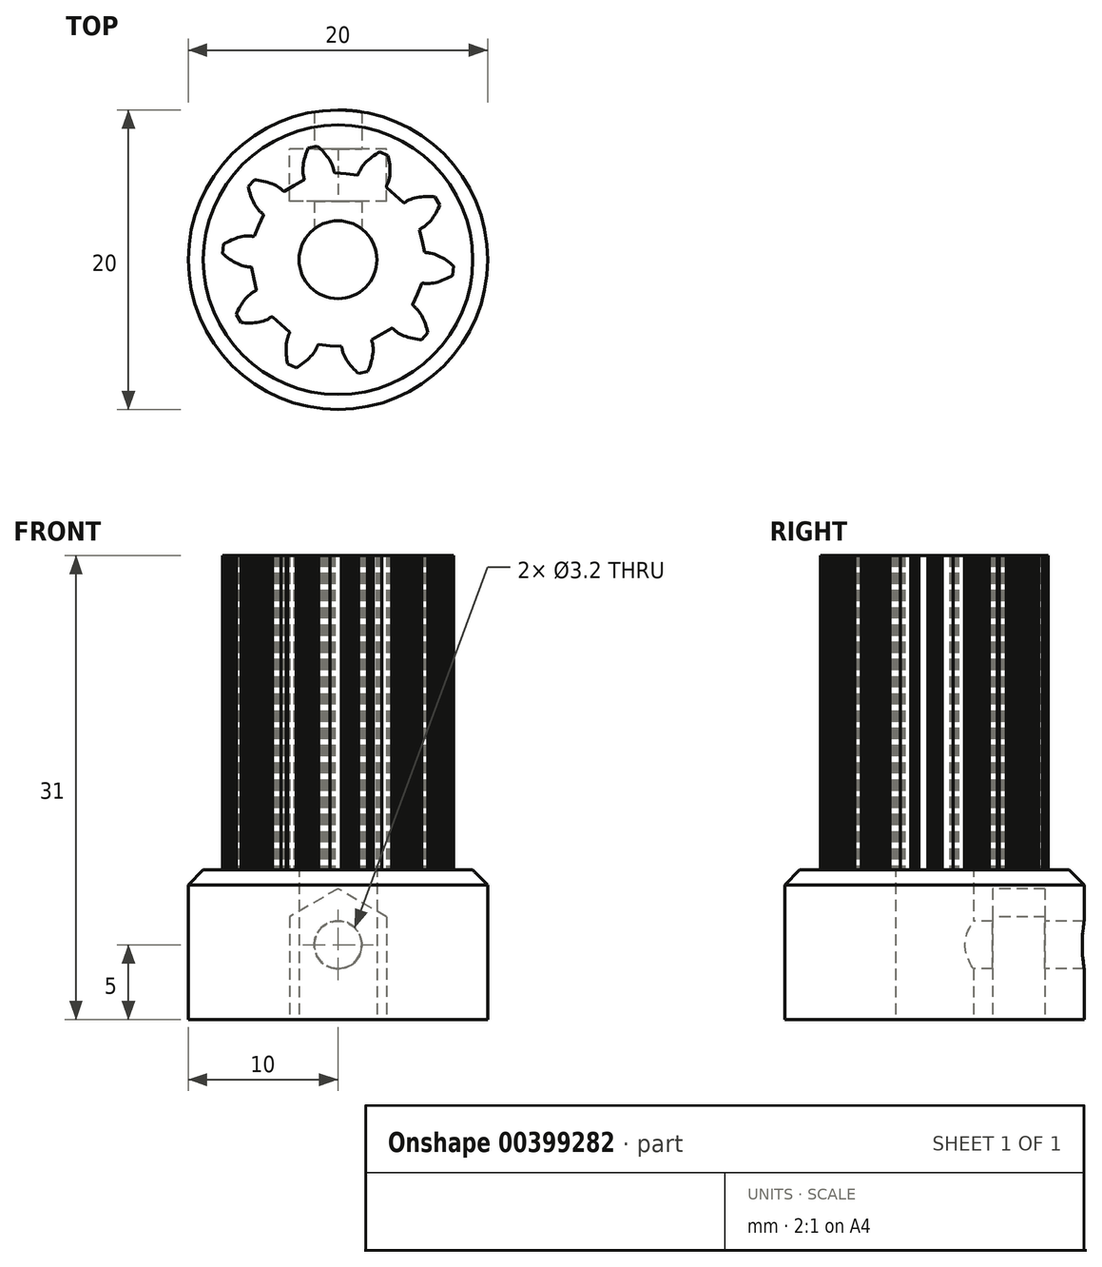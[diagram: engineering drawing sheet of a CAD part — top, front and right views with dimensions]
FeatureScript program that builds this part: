
annotation { "Feature Type Name" : "Feature", "Feature Type Description" : "" }
export const myFeature = defineFeature(function(context is Context, id is Id, definition is map)
    precondition{}
    {
        {
            var Q0;
            Q0=qCreatedBy(makeId("Top.planeOp"),FACE);
            var sketch = newSketch(context, id + "F0", { "sketchPlane" : qUnion([Q0])});
            skLineSegment(sketch, "E0", {"start": v(5.65, -3.86) * mm, "end": v(5.58, -3.73) * mm});
            skLineSegment(sketch, "E1", {"start": v(5.58, -3.73) * mm, "end": v(5.5, -3.6) * mm});
            skLineSegment(sketch, "E2", {"start": v(5.5, -3.6) * mm, "end": v(5.43, -3.49) * mm});
            skLineSegment(sketch, "E3", {"start": v(5.43, -3.49) * mm, "end": v(5.35, -3.37) * mm});
            skLineSegment(sketch, "E4", {"start": v(5.35, -3.37) * mm, "end": v(5.26, -3.27) * mm});
            skLineSegment(sketch, "E5", {"start": v(5.26, -3.27) * mm, "end": v(5.2, -3.22) * mm});
            skLineSegment(sketch, "E6", {"start": v(5.2, -3.22) * mm, "end": v(5.16, -3.18) * mm});
            skLineSegment(sketch, "E7", {"start": v(5.16, -3.18) * mm, "end": v(5.1, -3.14) * mm});
            skLineSegment(sketch, "E8", {"start": v(5.1, -3.14) * mm, "end": v(5.06, -3.1) * mm});
            skLineSegment(sketch, "E9", {"start": v(5.06, -3.1) * mm, "end": v(5.03, -3.07) * mm});
            skLineSegment(sketch, "E10", {"start": v(5.03, -3.07) * mm, "end": v(5.01, -3.05) * mm});
            skLineSegment(sketch, "E11", {"start": v(5.01, -3.05) * mm, "end": v(5, -3.02) * mm});
            skLineSegment(sketch, "E12", {"start": v(5, -3.02) * mm, "end": v(4.97, -2.98) * mm});
            skLineSegment(sketch, "E13", {"start": v(4.97, -2.98) * mm, "end": v(5.3, -2.3) * mm});
            skLineSegment(sketch, "E14", {"start": v(5.3, -2.3) * mm, "end": v(5.58, -1.58) * mm});
            skLineSegment(sketch, "E15", {"start": v(5.58, -1.58) * mm, "end": v(5.62, -1.57) * mm});
            skLineSegment(sketch, "E16", {"start": v(5.62, -1.57) * mm, "end": v(5.65, -1.57) * mm});
            skLineSegment(sketch, "E17", {"start": v(5.65, -1.57) * mm, "end": v(5.69, -1.57) * mm});
            skLineSegment(sketch, "E18", {"start": v(5.69, -1.57) * mm, "end": v(5.72, -1.57) * mm});
            skLineSegment(sketch, "E19", {"start": v(5.72, -1.57) * mm, "end": v(5.78, -1.58) * mm});
            skLineSegment(sketch, "E20", {"start": v(5.78, -1.58) * mm, "end": v(5.85, -1.59) * mm});
            skLineSegment(sketch, "E21", {"start": v(5.85, -1.59) * mm, "end": v(5.92, -1.6) * mm});
            skLineSegment(sketch, "E22", {"start": v(5.92, -1.6) * mm, "end": v(5.98, -1.6) * mm});
            skLineSegment(sketch, "E23", {"start": v(5.98, -1.6) * mm, "end": v(6.12, -1.59) * mm});
            skLineSegment(sketch, "E24", {"start": v(6.12, -1.59) * mm, "end": v(6.26, -1.57) * mm});
            skLineSegment(sketch, "E25", {"start": v(6.26, -1.57) * mm, "end": v(6.4, -1.55) * mm});
            skLineSegment(sketch, "E26", {"start": v(6.4, -1.55) * mm, "end": v(6.54, -1.52) * mm});
            skLineSegment(sketch, "E27", {"start": v(6.54, -1.52) * mm, "end": v(6.68, -1.48) * mm});
            skLineSegment(sketch, "E28", {"start": v(6.68, -1.48) * mm, "end": v(6.83, -1.43) * mm});
            skLineSegment(sketch, "E29", {"start": v(6.83, -1.43) * mm, "end": v(6.97, -1.38) * mm});
            skLineSegment(sketch, "E30", {"start": v(6.97, -1.38) * mm, "end": v(7.11, -1.32) * mm});
            skLineSegment(sketch, "E31", {"start": v(7.11, -1.32) * mm, "end": v(7.26, -1.25) * mm});
            skLineSegment(sketch, "E32", {"start": v(7.26, -1.25) * mm, "end": v(7.4, -1.18) * mm});
            skLineSegment(sketch, "E33", {"start": v(7.4, -1.18) * mm, "end": v(7.55, -1.1) * mm});
            skLineSegment(sketch, "E34", {"start": v(7.55, -1.1) * mm, "end": v(7.66, -1.03) * mm});
            skLineSegment(sketch, "E35", {"start": v(7.66, -1.03) * mm, "end": v(7.71, -0.42) * mm});
            skLineSegment(sketch, "E36", {"start": v(7.71, -0.42) * mm, "end": v(7.62, -0.34) * mm});
            skLineSegment(sketch, "E37", {"start": v(7.62, -0.34) * mm, "end": v(7.5, -0.23) * mm});
            skLineSegment(sketch, "E38", {"start": v(7.5, -0.23) * mm, "end": v(7.37, -0.13) * mm});
            skLineSegment(sketch, "E39", {"start": v(7.37, -0.13) * mm, "end": v(7.24, -0.04) * mm});
            skLineSegment(sketch, "E40", {"start": v(7.24, -0.04) * mm, "end": v(7.1, 0.05) * mm});
            skLineSegment(sketch, "E41", {"start": v(7.1, 0.05) * mm, "end": v(6.97, 0.13) * mm});
            skLineSegment(sketch, "E42", {"start": v(6.97, 0.13) * mm, "end": v(6.84, 0.2) * mm});
            skLineSegment(sketch, "E43", {"start": v(6.84, 0.2) * mm, "end": v(6.7, 0.27) * mm});
            skLineSegment(sketch, "E44", {"start": v(6.7, 0.27) * mm, "end": v(6.57, 0.32) * mm});
            skLineSegment(sketch, "E45", {"start": v(6.57, 0.32) * mm, "end": v(6.44, 0.37) * mm});
            skLineSegment(sketch, "E46", {"start": v(6.44, 0.37) * mm, "end": v(6.3, 0.41) * mm});
            skLineSegment(sketch, "E47", {"start": v(6.3, 0.41) * mm, "end": v(6.18, 0.44) * mm});
            skLineSegment(sketch, "E48", {"start": v(6.18, 0.44) * mm, "end": v(6.1, 0.45) * mm});
            skLineSegment(sketch, "E49", {"start": v(6.1, 0.45) * mm, "end": v(6.04, 0.46) * mm});
            skLineSegment(sketch, "E50", {"start": v(6.04, 0.46) * mm, "end": v(5.98, 0.47) * mm});
            skLineSegment(sketch, "E51", {"start": v(5.98, 0.47) * mm, "end": v(5.91, 0.47) * mm});
            skLineSegment(sketch, "E52", {"start": v(5.91, 0.47) * mm, "end": v(5.88, 0.47) * mm});
            skLineSegment(sketch, "E53", {"start": v(5.88, 0.47) * mm, "end": v(5.84, 0.48) * mm});
            skLineSegment(sketch, "E54", {"start": v(5.84, 0.48) * mm, "end": v(5.81, 0.5) * mm});
            skLineSegment(sketch, "E55", {"start": v(5.81, 0.5) * mm, "end": v(5.78, 0.51) * mm});
            skLineSegment(sketch, "E56", {"start": v(5.78, 0.51) * mm, "end": v(5.63, 1.26) * mm});
            skLineSegment(sketch, "E57", {"start": v(5.63, 1.26) * mm, "end": v(5.44, 2) * mm});
            skLineSegment(sketch, "E58", {"start": v(5.44, 2) * mm, "end": v(5.47, 2.03) * mm});
            skLineSegment(sketch, "E59", {"start": v(5.47, 2.03) * mm, "end": v(5.5, 2.05) * mm});
            skLineSegment(sketch, "E60", {"start": v(5.5, 2.05) * mm, "end": v(5.52, 2.07) * mm});
            skLineSegment(sketch, "E61", {"start": v(5.52, 2.07) * mm, "end": v(5.55, 2.1) * mm});
            skLineSegment(sketch, "E62", {"start": v(5.55, 2.1) * mm, "end": v(5.6, 2.12) * mm});
            skLineSegment(sketch, "E63", {"start": v(5.6, 2.12) * mm, "end": v(5.66, 2.15) * mm});
            skLineSegment(sketch, "E64", {"start": v(5.66, 2.15) * mm, "end": v(5.72, 2.19) * mm});
            skLineSegment(sketch, "E65", {"start": v(5.72, 2.19) * mm, "end": v(5.78, 2.23) * mm});
            skLineSegment(sketch, "E66", {"start": v(5.78, 2.23) * mm, "end": v(5.88, 2.31) * mm});
            skLineSegment(sketch, "E67", {"start": v(5.88, 2.31) * mm, "end": v(5.99, 2.4) * mm});
            skLineSegment(sketch, "E68", {"start": v(5.99, 2.4) * mm, "end": v(6.09, 2.5) * mm});
            skLineSegment(sketch, "E69", {"start": v(6.09, 2.5) * mm, "end": v(6.18, 2.62) * mm});
            skLineSegment(sketch, "E70", {"start": v(6.18, 2.62) * mm, "end": v(6.28, 2.73) * mm});
            skLineSegment(sketch, "E71", {"start": v(6.28, 2.73) * mm, "end": v(6.36, 2.85) * mm});
            skLineSegment(sketch, "E72", {"start": v(6.36, 2.85) * mm, "end": v(6.45, 2.98) * mm});
            skLineSegment(sketch, "E73", {"start": v(6.45, 2.98) * mm, "end": v(6.53, 3.12) * mm});
            skLineSegment(sketch, "E74", {"start": v(6.53, 3.12) * mm, "end": v(6.6, 3.25) * mm});
            skLineSegment(sketch, "E75", {"start": v(6.6, 3.25) * mm, "end": v(6.68, 3.4) * mm});
            skLineSegment(sketch, "E76", {"start": v(6.68, 3.4) * mm, "end": v(6.75, 3.55) * mm});
            skLineSegment(sketch, "E77", {"start": v(6.75, 3.55) * mm, "end": v(6.8, 3.66) * mm});
            skLineSegment(sketch, "E78", {"start": v(6.8, 3.66) * mm, "end": v(6.49, 4.2) * mm});
            skLineSegment(sketch, "E79", {"start": v(6.49, 4.2) * mm, "end": v(6.36, 4.2) * mm});
            skLineSegment(sketch, "E80", {"start": v(6.36, 4.2) * mm, "end": v(6.2, 4.22) * mm});
            skLineSegment(sketch, "E81", {"start": v(6.2, 4.22) * mm, "end": v(6.04, 4.22) * mm});
            skLineSegment(sketch, "E82", {"start": v(6.04, 4.22) * mm, "end": v(5.88, 4.22) * mm});
            skLineSegment(sketch, "E83", {"start": v(5.88, 4.22) * mm, "end": v(5.72, 4.22) * mm});
            skLineSegment(sketch, "E84", {"start": v(5.72, 4.22) * mm, "end": v(5.57, 4.2) * mm});
            skLineSegment(sketch, "E85", {"start": v(5.57, 4.2) * mm, "end": v(5.42, 4.18) * mm});
            skLineSegment(sketch, "E86", {"start": v(5.42, 4.18) * mm, "end": v(5.27, 4.16) * mm});
            skLineSegment(sketch, "E87", {"start": v(5.27, 4.16) * mm, "end": v(5.13, 4.13) * mm});
            skLineSegment(sketch, "E88", {"start": v(5.13, 4.13) * mm, "end": v(5, 4.09) * mm});
            skLineSegment(sketch, "E89", {"start": v(5, 4.09) * mm, "end": v(4.86, 4.04) * mm});
            skLineSegment(sketch, "E90", {"start": v(4.86, 4.04) * mm, "end": v(4.74, 3.99) * mm});
            skLineSegment(sketch, "E91", {"start": v(4.74, 3.99) * mm, "end": v(4.67, 3.96) * mm});
            skLineSegment(sketch, "E92", {"start": v(4.67, 3.96) * mm, "end": v(4.62, 3.93) * mm});
            skLineSegment(sketch, "E93", {"start": v(4.62, 3.93) * mm, "end": v(4.56, 3.89) * mm});
            skLineSegment(sketch, "E94", {"start": v(4.56, 3.89) * mm, "end": v(4.5, 3.85) * mm});
            skLineSegment(sketch, "E95", {"start": v(4.5, 3.85) * mm, "end": v(4.48, 3.84) * mm});
            skLineSegment(sketch, "E96", {"start": v(4.48, 3.84) * mm, "end": v(4.45, 3.82) * mm});
            skLineSegment(sketch, "E97", {"start": v(4.45, 3.82) * mm, "end": v(4.41, 3.81) * mm});
            skLineSegment(sketch, "E98", {"start": v(4.41, 3.81) * mm, "end": v(4.37, 3.8) * mm});
            skLineSegment(sketch, "E99", {"start": v(4.37, 3.8) * mm, "end": v(3.81, 4.33) * mm});
            skLineSegment(sketch, "E100", {"start": v(3.81, 4.33) * mm, "end": v(3.23, 4.82) * mm});
            skLineSegment(sketch, "E101", {"start": v(3.23, 4.82) * mm, "end": v(3.23, 4.86) * mm});
            skLineSegment(sketch, "E102", {"start": v(3.23, 4.86) * mm, "end": v(3.24, 4.9) * mm});
            skLineSegment(sketch, "E103", {"start": v(3.24, 4.9) * mm, "end": v(3.25, 4.92) * mm});
            skLineSegment(sketch, "E104", {"start": v(3.25, 4.92) * mm, "end": v(3.26, 4.95) * mm});
            skLineSegment(sketch, "E105", {"start": v(3.26, 4.95) * mm, "end": v(3.29, 5.01) * mm});
            skLineSegment(sketch, "E106", {"start": v(3.29, 5.01) * mm, "end": v(3.32, 5.07) * mm});
            skLineSegment(sketch, "E107", {"start": v(3.32, 5.07) * mm, "end": v(3.34, 5.13) * mm});
            skLineSegment(sketch, "E108", {"start": v(3.34, 5.13) * mm, "end": v(3.36, 5.2) * mm});
            skLineSegment(sketch, "E109", {"start": v(3.36, 5.2) * mm, "end": v(3.4, 5.33) * mm});
            skLineSegment(sketch, "E110", {"start": v(3.4, 5.33) * mm, "end": v(3.43, 5.47) * mm});
            skLineSegment(sketch, "E111", {"start": v(3.43, 5.47) * mm, "end": v(3.45, 5.6) * mm});
            skLineSegment(sketch, "E112", {"start": v(3.45, 5.6) * mm, "end": v(3.46, 5.75) * mm});
            skLineSegment(sketch, "E113", {"start": v(3.46, 5.75) * mm, "end": v(3.47, 5.9) * mm});
            skLineSegment(sketch, "E114", {"start": v(3.47, 5.9) * mm, "end": v(3.47, 6.05) * mm});
            skLineSegment(sketch, "E115", {"start": v(3.47, 6.05) * mm, "end": v(3.47, 6.2) * mm});
            skLineSegment(sketch, "E116", {"start": v(3.47, 6.2) * mm, "end": v(3.45, 6.36) * mm});
            skLineSegment(sketch, "E117", {"start": v(3.45, 6.36) * mm, "end": v(3.43, 6.52) * mm});
            skLineSegment(sketch, "E118", {"start": v(3.43, 6.52) * mm, "end": v(3.4, 6.68) * mm});
            skLineSegment(sketch, "E119", {"start": v(3.4, 6.68) * mm, "end": v(3.38, 6.84) * mm});
            skLineSegment(sketch, "E120", {"start": v(3.38, 6.84) * mm, "end": v(3.35, 6.96) * mm});
            skLineSegment(sketch, "E121", {"start": v(3.35, 6.96) * mm, "end": v(2.78, 7.2) * mm});
            skLineSegment(sketch, "E122", {"start": v(2.78, 7.2) * mm, "end": v(2.67, 7.14) * mm});
            skLineSegment(sketch, "E123", {"start": v(2.67, 7.14) * mm, "end": v(2.53, 7.06) * mm});
            skLineSegment(sketch, "E124", {"start": v(2.53, 7.06) * mm, "end": v(2.4, 6.96) * mm});
            skLineSegment(sketch, "E125", {"start": v(2.4, 6.96) * mm, "end": v(2.27, 6.87) * mm});
            skLineSegment(sketch, "E126", {"start": v(2.27, 6.87) * mm, "end": v(2.15, 6.77) * mm});
            skLineSegment(sketch, "E127", {"start": v(2.15, 6.77) * mm, "end": v(2.03, 6.67) * mm});
            skLineSegment(sketch, "E128", {"start": v(2.03, 6.67) * mm, "end": v(1.92, 6.57) * mm});
            skLineSegment(sketch, "E129", {"start": v(1.92, 6.57) * mm, "end": v(1.82, 6.46) * mm});
            skLineSegment(sketch, "E130", {"start": v(1.82, 6.46) * mm, "end": v(1.73, 6.35) * mm});
            skLineSegment(sketch, "E131", {"start": v(1.73, 6.35) * mm, "end": v(1.64, 6.24) * mm});
            skLineSegment(sketch, "E132", {"start": v(1.64, 6.24) * mm, "end": v(1.56, 6.13) * mm});
            skLineSegment(sketch, "E133", {"start": v(1.56, 6.13) * mm, "end": v(1.49, 6.01) * mm});
            skLineSegment(sketch, "E134", {"start": v(1.49, 6.01) * mm, "end": v(1.46, 5.95) * mm});
            skLineSegment(sketch, "E135", {"start": v(1.46, 5.95) * mm, "end": v(1.43, 5.89) * mm});
            skLineSegment(sketch, "E136", {"start": v(1.43, 5.89) * mm, "end": v(1.4, 5.83) * mm});
            skLineSegment(sketch, "E137", {"start": v(1.4, 5.83) * mm, "end": v(1.38, 5.77) * mm});
            skLineSegment(sketch, "E138", {"start": v(1.38, 5.77) * mm, "end": v(1.37, 5.74) * mm});
            skLineSegment(sketch, "E139", {"start": v(1.37, 5.74) * mm, "end": v(1.35, 5.7) * mm});
            skLineSegment(sketch, "E140", {"start": v(1.35, 5.7) * mm, "end": v(1.33, 5.68) * mm});
            skLineSegment(sketch, "E141", {"start": v(1.33, 5.68) * mm, "end": v(1.3, 5.65) * mm});
            skLineSegment(sketch, "E142", {"start": v(1.3, 5.65) * mm, "end": v(0.54, 5.74) * mm});
            skLineSegment(sketch, "E143", {"start": v(0.54, 5.74) * mm, "end": v(-0.22, 5.8) * mm});
            skLineSegment(sketch, "E144", {"start": v(-0.22, 5.8) * mm, "end": v(-0.24, 5.83) * mm});
            skLineSegment(sketch, "E145", {"start": v(-0.24, 5.83) * mm, "end": v(-0.26, 5.86) * mm});
            skLineSegment(sketch, "E146", {"start": v(-0.26, 5.86) * mm, "end": v(-0.27, 5.9) * mm});
            skLineSegment(sketch, "E147", {"start": v(-0.27, 5.9) * mm, "end": v(-0.28, 5.92) * mm});
            skLineSegment(sketch, "E148", {"start": v(-0.28, 5.92) * mm, "end": v(-0.29, 5.99) * mm});
            skLineSegment(sketch, "E149", {"start": v(-0.29, 5.99) * mm, "end": v(-0.3, 6.05) * mm});
            skLineSegment(sketch, "E150", {"start": v(-0.3, 6.05) * mm, "end": v(-0.31, 6.12) * mm});
            skLineSegment(sketch, "E151", {"start": v(-0.31, 6.12) * mm, "end": v(-0.33, 6.18) * mm});
            skLineSegment(sketch, "E152", {"start": v(-0.33, 6.18) * mm, "end": v(-0.38, 6.31) * mm});
            skLineSegment(sketch, "E153", {"start": v(-0.38, 6.31) * mm, "end": v(-0.44, 6.44) * mm});
            skLineSegment(sketch, "E154", {"start": v(-0.44, 6.44) * mm, "end": v(-0.5, 6.56) * mm});
            skLineSegment(sketch, "E155", {"start": v(-0.5, 6.56) * mm, "end": v(-0.58, 6.69) * mm});
            skLineSegment(sketch, "E156", {"start": v(-0.58, 6.69) * mm, "end": v(-0.66, 6.81) * mm});
            skLineSegment(sketch, "E157", {"start": v(-0.66, 6.81) * mm, "end": v(-0.75, 6.93) * mm});
            skLineSegment(sketch, "E158", {"start": v(-0.75, 6.93) * mm, "end": v(-0.84, 7.06) * mm});
            skLineSegment(sketch, "E159", {"start": v(-0.84, 7.06) * mm, "end": v(-0.94, 7.17) * mm});
            skLineSegment(sketch, "E160", {"start": v(-0.94, 7.17) * mm, "end": v(-1.05, 7.3) * mm});
            skLineSegment(sketch, "E161", {"start": v(-1.05, 7.3) * mm, "end": v(-1.17, 7.4) * mm});
            skLineSegment(sketch, "E162", {"start": v(-1.17, 7.4) * mm, "end": v(-1.29, 7.52) * mm});
            skLineSegment(sketch, "E163", {"start": v(-1.29, 7.52) * mm, "end": v(-1.38, 7.6) * mm});
            skLineSegment(sketch, "E164", {"start": v(-1.38, 7.6) * mm, "end": v(-1.98, 7.47) * mm});
            skLineSegment(sketch, "E165", {"start": v(-1.98, 7.47) * mm, "end": v(-2.04, 7.35) * mm});
            skLineSegment(sketch, "E166", {"start": v(-2.04, 7.35) * mm, "end": v(-2.1, 7.2) * mm});
            skLineSegment(sketch, "E167", {"start": v(-2.1, 7.2) * mm, "end": v(-2.15, 7.05) * mm});
            skLineSegment(sketch, "E168", {"start": v(-2.15, 7.05) * mm, "end": v(-2.2, 6.9) * mm});
            skLineSegment(sketch, "E169", {"start": v(-2.2, 6.9) * mm, "end": v(-2.24, 6.74) * mm});
            skLineSegment(sketch, "E170", {"start": v(-2.24, 6.74) * mm, "end": v(-2.28, 6.6) * mm});
            skLineSegment(sketch, "E171", {"start": v(-2.28, 6.6) * mm, "end": v(-2.3, 6.44) * mm});
            skLineSegment(sketch, "E172", {"start": v(-2.3, 6.44) * mm, "end": v(-2.33, 6.3) * mm});
            skLineSegment(sketch, "E173", {"start": v(-2.33, 6.3) * mm, "end": v(-2.34, 6.15) * mm});
            skLineSegment(sketch, "E174", {"start": v(-2.34, 6.15) * mm, "end": v(-2.34, 6.01) * mm});
            skLineSegment(sketch, "E175", {"start": v(-2.34, 6.01) * mm, "end": v(-2.34, 5.87) * mm});
            skLineSegment(sketch, "E176", {"start": v(-2.34, 5.87) * mm, "end": v(-2.33, 5.74) * mm});
            skLineSegment(sketch, "E177", {"start": v(-2.33, 5.74) * mm, "end": v(-2.32, 5.67) * mm});
            skLineSegment(sketch, "E178", {"start": v(-2.32, 5.67) * mm, "end": v(-2.3, 5.6) * mm});
            skLineSegment(sketch, "E179", {"start": v(-2.3, 5.6) * mm, "end": v(-2.29, 5.54) * mm});
            skLineSegment(sketch, "E180", {"start": v(-2.29, 5.54) * mm, "end": v(-2.27, 5.48) * mm});
            skLineSegment(sketch, "E181", {"start": v(-2.27, 5.48) * mm, "end": v(-2.27, 5.44) * mm});
            skLineSegment(sketch, "E182", {"start": v(-2.27, 5.44) * mm, "end": v(-2.26, 5.41) * mm});
            skLineSegment(sketch, "E183", {"start": v(-2.26, 5.41) * mm, "end": v(-2.26, 5.37) * mm});
            skLineSegment(sketch, "E184", {"start": v(-2.26, 5.37) * mm, "end": v(-2.27, 5.34) * mm});
            skLineSegment(sketch, "E185", {"start": v(-2.27, 5.34) * mm, "end": v(-2.94, 4.96) * mm});
            skLineSegment(sketch, "E186", {"start": v(-2.94, 4.96) * mm, "end": v(-3.58, 4.56) * mm});
            skLineSegment(sketch, "E187", {"start": v(-3.58, 4.56) * mm, "end": v(-3.62, 4.57) * mm});
            skLineSegment(sketch, "E188", {"start": v(-3.62, 4.57) * mm, "end": v(-3.65, 4.59) * mm});
            skLineSegment(sketch, "E189", {"start": v(-3.65, 4.59) * mm, "end": v(-3.68, 4.6) * mm});
            skLineSegment(sketch, "E190", {"start": v(-3.68, 4.6) * mm, "end": v(-3.7, 4.63) * mm});
            skLineSegment(sketch, "E191", {"start": v(-3.7, 4.63) * mm, "end": v(-3.75, 4.68) * mm});
            skLineSegment(sketch, "E192", {"start": v(-3.75, 4.68) * mm, "end": v(-3.8, 4.72) * mm});
            skLineSegment(sketch, "E193", {"start": v(-3.8, 4.72) * mm, "end": v(-3.85, 4.76) * mm});
            skLineSegment(sketch, "E194", {"start": v(-3.85, 4.76) * mm, "end": v(-3.9, 4.8) * mm});
            skLineSegment(sketch, "E195", {"start": v(-3.9, 4.8) * mm, "end": v(-4.02, 4.88) * mm});
            skLineSegment(sketch, "E196", {"start": v(-4.02, 4.88) * mm, "end": v(-4.14, 4.95) * mm});
            skLineSegment(sketch, "E197", {"start": v(-4.14, 4.95) * mm, "end": v(-4.27, 5.01) * mm});
            skLineSegment(sketch, "E198", {"start": v(-4.27, 5.01) * mm, "end": v(-4.4, 5.07) * mm});
            skLineSegment(sketch, "E199", {"start": v(-4.4, 5.07) * mm, "end": v(-4.54, 5.12) * mm});
            skLineSegment(sketch, "E200", {"start": v(-4.54, 5.12) * mm, "end": v(-4.68, 5.17) * mm});
            skLineSegment(sketch, "E201", {"start": v(-4.68, 5.17) * mm, "end": v(-4.83, 5.21) * mm});
            skLineSegment(sketch, "E202", {"start": v(-4.83, 5.21) * mm, "end": v(-4.98, 5.25) * mm});
            skLineSegment(sketch, "E203", {"start": v(-4.98, 5.25) * mm, "end": v(-5.14, 5.28) * mm});
            skLineSegment(sketch, "E204", {"start": v(-5.14, 5.28) * mm, "end": v(-5.3, 5.3) * mm});
            skLineSegment(sketch, "E205", {"start": v(-5.3, 5.3) * mm, "end": v(-5.46, 5.32) * mm});
            skLineSegment(sketch, "E206", {"start": v(-5.46, 5.32) * mm, "end": v(-5.59, 5.34) * mm});
            skLineSegment(sketch, "E207", {"start": v(-5.59, 5.34) * mm, "end": v(-6, 4.87) * mm});
            skLineSegment(sketch, "E208", {"start": v(-6, 4.87) * mm, "end": v(-5.97, 4.75) * mm});
            skLineSegment(sketch, "E209", {"start": v(-5.97, 4.75) * mm, "end": v(-5.93, 4.6) * mm});
            skLineSegment(sketch, "E210", {"start": v(-5.93, 4.6) * mm, "end": v(-5.88, 4.44) * mm});
            skLineSegment(sketch, "E211", {"start": v(-5.88, 4.44) * mm, "end": v(-5.83, 4.28) * mm});
            skLineSegment(sketch, "E212", {"start": v(-5.83, 4.28) * mm, "end": v(-5.78, 4.14) * mm});
            skLineSegment(sketch, "E213", {"start": v(-5.78, 4.14) * mm, "end": v(-5.72, 4) * mm});
            skLineSegment(sketch, "E214", {"start": v(-5.72, 4) * mm, "end": v(-5.65, 3.86) * mm});
            skLineSegment(sketch, "E215", {"start": v(-5.65, 3.86) * mm, "end": v(-5.58, 3.73) * mm});
            skLineSegment(sketch, "E216", {"start": v(-5.58, 3.73) * mm, "end": v(-5.5, 3.6) * mm});
            skLineSegment(sketch, "E217", {"start": v(-5.5, 3.6) * mm, "end": v(-5.43, 3.49) * mm});
            skLineSegment(sketch, "E218", {"start": v(-5.43, 3.49) * mm, "end": v(-5.35, 3.37) * mm});
            skLineSegment(sketch, "E219", {"start": v(-5.35, 3.37) * mm, "end": v(-5.26, 3.27) * mm});
            skLineSegment(sketch, "E220", {"start": v(-5.26, 3.27) * mm, "end": v(-5.2, 3.22) * mm});
            skLineSegment(sketch, "E221", {"start": v(-5.2, 3.22) * mm, "end": v(-5.16, 3.18) * mm});
            skLineSegment(sketch, "E222", {"start": v(-5.16, 3.18) * mm, "end": v(-5.1, 3.14) * mm});
            skLineSegment(sketch, "E223", {"start": v(-5.1, 3.14) * mm, "end": v(-5.06, 3.1) * mm});
            skLineSegment(sketch, "E224", {"start": v(-5.06, 3.1) * mm, "end": v(-5.03, 3.07) * mm});
            skLineSegment(sketch, "E225", {"start": v(-5.03, 3.07) * mm, "end": v(-5.01, 3.05) * mm});
            skLineSegment(sketch, "E226", {"start": v(-5.01, 3.05) * mm, "end": v(-5, 3.02) * mm});
            skLineSegment(sketch, "E227", {"start": v(-5, 3.02) * mm, "end": v(-4.97, 2.98) * mm});
            skLineSegment(sketch, "E228", {"start": v(-4.97, 2.98) * mm, "end": v(-5.3, 2.3) * mm});
            skLineSegment(sketch, "E229", {"start": v(-5.3, 2.3) * mm, "end": v(-5.58, 1.58) * mm});
            skLineSegment(sketch, "E230", {"start": v(-5.58, 1.58) * mm, "end": v(-5.62, 1.57) * mm});
            skLineSegment(sketch, "E231", {"start": v(-5.62, 1.57) * mm, "end": v(-5.65, 1.57) * mm});
            skLineSegment(sketch, "E232", {"start": v(-5.65, 1.57) * mm, "end": v(-5.69, 1.57) * mm});
            skLineSegment(sketch, "E233", {"start": v(-5.69, 1.57) * mm, "end": v(-5.72, 1.57) * mm});
            skLineSegment(sketch, "E234", {"start": v(-5.72, 1.57) * mm, "end": v(-5.78, 1.58) * mm});
            skLineSegment(sketch, "E235", {"start": v(-5.78, 1.58) * mm, "end": v(-5.85, 1.59) * mm});
            skLineSegment(sketch, "E236", {"start": v(-5.85, 1.59) * mm, "end": v(-5.92, 1.6) * mm});
            skLineSegment(sketch, "E237", {"start": v(-5.92, 1.6) * mm, "end": v(-5.98, 1.6) * mm});
            skLineSegment(sketch, "E238", {"start": v(-5.98, 1.6) * mm, "end": v(-6.12, 1.59) * mm});
            skLineSegment(sketch, "E239", {"start": v(-6.12, 1.59) * mm, "end": v(-6.26, 1.57) * mm});
            skLineSegment(sketch, "E240", {"start": v(-6.26, 1.57) * mm, "end": v(-6.4, 1.55) * mm});
            skLineSegment(sketch, "E241", {"start": v(-6.4, 1.55) * mm, "end": v(-6.54, 1.52) * mm});
            skLineSegment(sketch, "E242", {"start": v(-6.54, 1.52) * mm, "end": v(-6.68, 1.48) * mm});
            skLineSegment(sketch, "E243", {"start": v(-6.68, 1.48) * mm, "end": v(-6.83, 1.43) * mm});
            skLineSegment(sketch, "E244", {"start": v(-6.83, 1.43) * mm, "end": v(-6.97, 1.38) * mm});
            skLineSegment(sketch, "E245", {"start": v(-6.97, 1.38) * mm, "end": v(-7.11, 1.32) * mm});
            skLineSegment(sketch, "E246", {"start": v(-7.11, 1.32) * mm, "end": v(-7.26, 1.25) * mm});
            skLineSegment(sketch, "E247", {"start": v(-7.26, 1.25) * mm, "end": v(-7.4, 1.18) * mm});
            skLineSegment(sketch, "E248", {"start": v(-7.4, 1.18) * mm, "end": v(-7.55, 1.1) * mm});
            skLineSegment(sketch, "E249", {"start": v(-7.55, 1.1) * mm, "end": v(-7.66, 1.03) * mm});
            skLineSegment(sketch, "E250", {"start": v(-7.66, 1.03) * mm, "end": v(-7.71, 0.42) * mm});
            skLineSegment(sketch, "E251", {"start": v(-7.71, 0.42) * mm, "end": v(-7.62, 0.34) * mm});
            skLineSegment(sketch, "E252", {"start": v(-7.62, 0.34) * mm, "end": v(-7.5, 0.23) * mm});
            skLineSegment(sketch, "E253", {"start": v(-7.5, 0.23) * mm, "end": v(-7.37, 0.13) * mm});
            skLineSegment(sketch, "E254", {"start": v(-7.37, 0.13) * mm, "end": v(-7.24, 0.04) * mm});
            skLineSegment(sketch, "E255", {"start": v(-7.24, 0.04) * mm, "end": v(-7.1, -0.05) * mm});
            skLineSegment(sketch, "E256", {"start": v(-7.1, -0.05) * mm, "end": v(-6.97, -0.13) * mm});
            skLineSegment(sketch, "E257", {"start": v(-6.97, -0.13) * mm, "end": v(-6.84, -0.2) * mm});
            skLineSegment(sketch, "E258", {"start": v(-6.84, -0.2) * mm, "end": v(-6.7, -0.27) * mm});
            skLineSegment(sketch, "E259", {"start": v(-6.7, -0.27) * mm, "end": v(-6.58, -0.32) * mm});
            skLineSegment(sketch, "E260", {"start": v(-6.58, -0.32) * mm, "end": v(-6.44, -0.37) * mm});
            skLineSegment(sketch, "E261", {"start": v(-6.44, -0.37) * mm, "end": v(-6.3, -0.41) * mm});
            skLineSegment(sketch, "E262", {"start": v(-6.3, -0.41) * mm, "end": v(-6.18, -0.44) * mm});
            skLineSegment(sketch, "E263", {"start": v(-6.18, -0.44) * mm, "end": v(-6.1, -0.45) * mm});
            skLineSegment(sketch, "E264", {"start": v(-6.1, -0.45) * mm, "end": v(-6.04, -0.46) * mm});
            skLineSegment(sketch, "E265", {"start": v(-6.04, -0.46) * mm, "end": v(-5.98, -0.46) * mm});
            skLineSegment(sketch, "E266", {"start": v(-5.98, -0.46) * mm, "end": v(-5.91, -0.47) * mm});
            skLineSegment(sketch, "E267", {"start": v(-5.91, -0.47) * mm, "end": v(-5.88, -0.47) * mm});
            skLineSegment(sketch, "E268", {"start": v(-5.88, -0.47) * mm, "end": v(-5.84, -0.48) * mm});
            skLineSegment(sketch, "E269", {"start": v(-5.84, -0.48) * mm, "end": v(-5.81, -0.5) * mm});
            skLineSegment(sketch, "E270", {"start": v(-5.81, -0.5) * mm, "end": v(-5.78, -0.51) * mm});
            skLineSegment(sketch, "E271", {"start": v(-5.78, -0.51) * mm, "end": v(-5.63, -1.26) * mm});
            skLineSegment(sketch, "E272", {"start": v(-5.63, -1.26) * mm, "end": v(-5.44, -2) * mm});
            skLineSegment(sketch, "E273", {"start": v(-5.44, -2) * mm, "end": v(-5.47, -2.03) * mm});
            skLineSegment(sketch, "E274", {"start": v(-5.47, -2.03) * mm, "end": v(-5.5, -2.05) * mm});
            skLineSegment(sketch, "E275", {"start": v(-5.5, -2.05) * mm, "end": v(-5.52, -2.07) * mm});
            skLineSegment(sketch, "E276", {"start": v(-5.52, -2.07) * mm, "end": v(-5.55, -2.1) * mm});
            skLineSegment(sketch, "E277", {"start": v(-5.55, -2.1) * mm, "end": v(-5.6, -2.12) * mm});
            skLineSegment(sketch, "E278", {"start": v(-5.6, -2.12) * mm, "end": v(-5.66, -2.15) * mm});
            skLineSegment(sketch, "E279", {"start": v(-5.66, -2.15) * mm, "end": v(-5.72, -2.19) * mm});
            skLineSegment(sketch, "E280", {"start": v(-5.72, -2.19) * mm, "end": v(-5.78, -2.23) * mm});
            skLineSegment(sketch, "E281", {"start": v(-5.78, -2.23) * mm, "end": v(-5.88, -2.31) * mm});
            skLineSegment(sketch, "E282", {"start": v(-5.88, -2.31) * mm, "end": v(-5.99, -2.4) * mm});
            skLineSegment(sketch, "E283", {"start": v(-5.99, -2.4) * mm, "end": v(-6.09, -2.5) * mm});
            skLineSegment(sketch, "E284", {"start": v(-6.09, -2.5) * mm, "end": v(-6.18, -2.62) * mm});
            skLineSegment(sketch, "E285", {"start": v(-6.18, -2.62) * mm, "end": v(-6.28, -2.73) * mm});
            skLineSegment(sketch, "E286", {"start": v(-6.28, -2.73) * mm, "end": v(-6.36, -2.85) * mm});
            skLineSegment(sketch, "E287", {"start": v(-6.36, -2.85) * mm, "end": v(-6.45, -2.98) * mm});
            skLineSegment(sketch, "E288", {"start": v(-6.45, -2.98) * mm, "end": v(-6.53, -3.12) * mm});
            skLineSegment(sketch, "E289", {"start": v(-6.53, -3.12) * mm, "end": v(-6.6, -3.25) * mm});
            skLineSegment(sketch, "E290", {"start": v(-6.6, -3.25) * mm, "end": v(-6.68, -3.4) * mm});
            skLineSegment(sketch, "E291", {"start": v(-6.68, -3.4) * mm, "end": v(-6.75, -3.55) * mm});
            skLineSegment(sketch, "E292", {"start": v(-6.75, -3.55) * mm, "end": v(-6.8, -3.66) * mm});
            skLineSegment(sketch, "E293", {"start": v(-6.8, -3.66) * mm, "end": v(-6.49, -4.2) * mm});
            skLineSegment(sketch, "E294", {"start": v(-6.49, -4.2) * mm, "end": v(-6.36, -4.2) * mm});
            skLineSegment(sketch, "E295", {"start": v(-6.36, -4.2) * mm, "end": v(-6.2, -4.22) * mm});
            skLineSegment(sketch, "E296", {"start": v(-6.2, -4.22) * mm, "end": v(-6.04, -4.22) * mm});
            skLineSegment(sketch, "E297", {"start": v(-6.04, -4.22) * mm, "end": v(-5.88, -4.22) * mm});
            skLineSegment(sketch, "E298", {"start": v(-5.88, -4.22) * mm, "end": v(-5.72, -4.22) * mm});
            skLineSegment(sketch, "E299", {"start": v(-5.72, -4.22) * mm, "end": v(-5.57, -4.2) * mm});
            skLineSegment(sketch, "E300", {"start": v(-5.57, -4.2) * mm, "end": v(-5.42, -4.18) * mm});
            skLineSegment(sketch, "E301", {"start": v(-5.42, -4.18) * mm, "end": v(-5.27, -4.16) * mm});
            skLineSegment(sketch, "E302", {"start": v(-5.27, -4.16) * mm, "end": v(-5.13, -4.13) * mm});
            skLineSegment(sketch, "E303", {"start": v(-5.13, -4.13) * mm, "end": v(-5, -4.09) * mm});
            skLineSegment(sketch, "E304", {"start": v(-5, -4.09) * mm, "end": v(-4.86, -4.04) * mm});
            skLineSegment(sketch, "E305", {"start": v(-4.86, -4.04) * mm, "end": v(-4.74, -3.99) * mm});
            skLineSegment(sketch, "E306", {"start": v(-4.74, -3.99) * mm, "end": v(-4.68, -3.96) * mm});
            skLineSegment(sketch, "E307", {"start": v(-4.68, -3.96) * mm, "end": v(-4.62, -3.93) * mm});
            skLineSegment(sketch, "E308", {"start": v(-4.62, -3.93) * mm, "end": v(-4.56, -3.89) * mm});
            skLineSegment(sketch, "E309", {"start": v(-4.56, -3.89) * mm, "end": v(-4.5, -3.85) * mm});
            skLineSegment(sketch, "E310", {"start": v(-4.5, -3.85) * mm, "end": v(-4.48, -3.84) * mm});
            skLineSegment(sketch, "E311", {"start": v(-4.48, -3.84) * mm, "end": v(-4.45, -3.82) * mm});
            skLineSegment(sketch, "E312", {"start": v(-4.45, -3.82) * mm, "end": v(-4.41, -3.81) * mm});
            skLineSegment(sketch, "E313", {"start": v(-4.41, -3.81) * mm, "end": v(-4.37, -3.8) * mm});
            skLineSegment(sketch, "E314", {"start": v(-4.37, -3.8) * mm, "end": v(-3.81, -4.33) * mm});
            skLineSegment(sketch, "E315", {"start": v(-3.81, -4.33) * mm, "end": v(-3.23, -4.82) * mm});
            skLineSegment(sketch, "E316", {"start": v(-3.23, -4.82) * mm, "end": v(-3.23, -4.86) * mm});
            skLineSegment(sketch, "E317", {"start": v(-3.23, -4.86) * mm, "end": v(-3.24, -4.9) * mm});
            skLineSegment(sketch, "E318", {"start": v(-3.24, -4.9) * mm, "end": v(-3.25, -4.92) * mm});
            skLineSegment(sketch, "E319", {"start": v(-3.25, -4.92) * mm, "end": v(-3.26, -4.95) * mm});
            skLineSegment(sketch, "E320", {"start": v(-3.26, -4.95) * mm, "end": v(-3.29, -5.01) * mm});
            skLineSegment(sketch, "E321", {"start": v(-3.29, -5.01) * mm, "end": v(-3.32, -5.07) * mm});
            skLineSegment(sketch, "E322", {"start": v(-3.32, -5.07) * mm, "end": v(-3.34, -5.13) * mm});
            skLineSegment(sketch, "E323", {"start": v(-3.34, -5.13) * mm, "end": v(-3.36, -5.2) * mm});
            skLineSegment(sketch, "E324", {"start": v(-3.36, -5.2) * mm, "end": v(-3.4, -5.33) * mm});
            skLineSegment(sketch, "E325", {"start": v(-3.4, -5.33) * mm, "end": v(-3.43, -5.47) * mm});
            skLineSegment(sketch, "E326", {"start": v(-3.43, -5.47) * mm, "end": v(-3.45, -5.6) * mm});
            skLineSegment(sketch, "E327", {"start": v(-3.45, -5.6) * mm, "end": v(-3.46, -5.75) * mm});
            skLineSegment(sketch, "E328", {"start": v(-3.46, -5.75) * mm, "end": v(-3.47, -5.9) * mm});
            skLineSegment(sketch, "E329", {"start": v(-3.47, -5.9) * mm, "end": v(-3.47, -6.05) * mm});
            skLineSegment(sketch, "E330", {"start": v(-3.47, -6.05) * mm, "end": v(-3.47, -6.2) * mm});
            skLineSegment(sketch, "E331", {"start": v(-3.47, -6.2) * mm, "end": v(-3.45, -6.36) * mm});
            skLineSegment(sketch, "E332", {"start": v(-3.45, -6.36) * mm, "end": v(-3.43, -6.52) * mm});
            skLineSegment(sketch, "E333", {"start": v(-3.43, -6.52) * mm, "end": v(-3.4, -6.68) * mm});
            skLineSegment(sketch, "E334", {"start": v(-3.4, -6.68) * mm, "end": v(-3.38, -6.84) * mm});
            skLineSegment(sketch, "E335", {"start": v(-3.38, -6.84) * mm, "end": v(-3.35, -6.96) * mm});
            skLineSegment(sketch, "E336", {"start": v(-3.35, -6.96) * mm, "end": v(-2.78, -7.2) * mm});
            skLineSegment(sketch, "E337", {"start": v(-2.78, -7.2) * mm, "end": v(-2.67, -7.14) * mm});
            skLineSegment(sketch, "E338", {"start": v(-2.67, -7.14) * mm, "end": v(-2.53, -7.06) * mm});
            skLineSegment(sketch, "E339", {"start": v(-2.53, -7.06) * mm, "end": v(-2.4, -6.96) * mm});
            skLineSegment(sketch, "E340", {"start": v(-2.4, -6.96) * mm, "end": v(-2.27, -6.87) * mm});
            skLineSegment(sketch, "E341", {"start": v(-2.27, -6.87) * mm, "end": v(-2.15, -6.77) * mm});
            skLineSegment(sketch, "E342", {"start": v(-2.15, -6.77) * mm, "end": v(-2.03, -6.67) * mm});
            skLineSegment(sketch, "E343", {"start": v(-2.03, -6.67) * mm, "end": v(-1.92, -6.57) * mm});
            skLineSegment(sketch, "E344", {"start": v(-1.92, -6.57) * mm, "end": v(-1.82, -6.46) * mm});
            skLineSegment(sketch, "E345", {"start": v(-1.82, -6.46) * mm, "end": v(-1.73, -6.35) * mm});
            skLineSegment(sketch, "E346", {"start": v(-1.73, -6.35) * mm, "end": v(-1.64, -6.24) * mm});
            skLineSegment(sketch, "E347", {"start": v(-1.64, -6.24) * mm, "end": v(-1.56, -6.13) * mm});
            skLineSegment(sketch, "E348", {"start": v(-1.56, -6.13) * mm, "end": v(-1.49, -6) * mm});
            skLineSegment(sketch, "E349", {"start": v(-1.49, -6) * mm, "end": v(-1.46, -5.95) * mm});
            skLineSegment(sketch, "E350", {"start": v(-1.46, -5.95) * mm, "end": v(-1.43, -5.89) * mm});
            skLineSegment(sketch, "E351", {"start": v(-1.43, -5.89) * mm, "end": v(-1.4, -5.83) * mm});
            skLineSegment(sketch, "E352", {"start": v(-1.4, -5.83) * mm, "end": v(-1.38, -5.77) * mm});
            skLineSegment(sketch, "E353", {"start": v(-1.38, -5.77) * mm, "end": v(-1.37, -5.74) * mm});
            skLineSegment(sketch, "E354", {"start": v(-1.37, -5.74) * mm, "end": v(-1.35, -5.7) * mm});
            skLineSegment(sketch, "E355", {"start": v(-1.35, -5.7) * mm, "end": v(-1.33, -5.68) * mm});
            skLineSegment(sketch, "E356", {"start": v(-1.33, -5.68) * mm, "end": v(-1.3, -5.65) * mm});
            skLineSegment(sketch, "E357", {"start": v(-1.3, -5.65) * mm, "end": v(-0.54, -5.74) * mm});
            skLineSegment(sketch, "E358", {"start": v(-0.54, -5.74) * mm, "end": v(0.22, -5.8) * mm});
            skLineSegment(sketch, "E359", {"start": v(0.22, -5.8) * mm, "end": v(0.24, -5.83) * mm});
            skLineSegment(sketch, "E360", {"start": v(0.24, -5.83) * mm, "end": v(0.26, -5.86) * mm});
            skLineSegment(sketch, "E361", {"start": v(0.26, -5.86) * mm, "end": v(0.27, -5.9) * mm});
            skLineSegment(sketch, "E362", {"start": v(0.27, -5.9) * mm, "end": v(0.28, -5.92) * mm});
            skLineSegment(sketch, "E363", {"start": v(0.28, -5.92) * mm, "end": v(0.29, -5.99) * mm});
            skLineSegment(sketch, "E364", {"start": v(0.29, -5.99) * mm, "end": v(0.3, -6.05) * mm});
            skLineSegment(sketch, "E365", {"start": v(0.3, -6.05) * mm, "end": v(0.31, -6.12) * mm});
            skLineSegment(sketch, "E366", {"start": v(0.31, -6.12) * mm, "end": v(0.33, -6.18) * mm});
            skLineSegment(sketch, "E367", {"start": v(0.33, -6.18) * mm, "end": v(0.38, -6.31) * mm});
            skLineSegment(sketch, "E368", {"start": v(0.38, -6.31) * mm, "end": v(0.44, -6.44) * mm});
            skLineSegment(sketch, "E369", {"start": v(0.44, -6.44) * mm, "end": v(0.5, -6.56) * mm});
            skLineSegment(sketch, "E370", {"start": v(0.5, -6.56) * mm, "end": v(0.58, -6.69) * mm});
            skLineSegment(sketch, "E371", {"start": v(0.58, -6.69) * mm, "end": v(0.66, -6.81) * mm});
            skLineSegment(sketch, "E372", {"start": v(0.66, -6.81) * mm, "end": v(0.75, -6.93) * mm});
            skLineSegment(sketch, "E373", {"start": v(0.75, -6.93) * mm, "end": v(0.84, -7.06) * mm});
            skLineSegment(sketch, "E374", {"start": v(0.84, -7.06) * mm, "end": v(0.94, -7.17) * mm});
            skLineSegment(sketch, "E375", {"start": v(0.94, -7.17) * mm, "end": v(1.05, -7.3) * mm});
            skLineSegment(sketch, "E376", {"start": v(1.05, -7.3) * mm, "end": v(1.17, -7.4) * mm});
            skLineSegment(sketch, "E377", {"start": v(1.17, -7.4) * mm, "end": v(1.29, -7.52) * mm});
            skLineSegment(sketch, "E378", {"start": v(1.29, -7.52) * mm, "end": v(1.38, -7.6) * mm});
            skLineSegment(sketch, "E379", {"start": v(1.38, -7.6) * mm, "end": v(1.98, -7.47) * mm});
            skLineSegment(sketch, "E380", {"start": v(1.98, -7.47) * mm, "end": v(2.04, -7.35) * mm});
            skLineSegment(sketch, "E381", {"start": v(2.04, -7.35) * mm, "end": v(2.1, -7.2) * mm});
            skLineSegment(sketch, "E382", {"start": v(2.1, -7.2) * mm, "end": v(2.15, -7.05) * mm});
            skLineSegment(sketch, "E383", {"start": v(2.15, -7.05) * mm, "end": v(2.2, -6.9) * mm});
            skLineSegment(sketch, "E384", {"start": v(2.2, -6.9) * mm, "end": v(2.24, -6.74) * mm});
            skLineSegment(sketch, "E385", {"start": v(2.24, -6.74) * mm, "end": v(2.28, -6.6) * mm});
            skLineSegment(sketch, "E386", {"start": v(2.28, -6.6) * mm, "end": v(2.3, -6.44) * mm});
            skLineSegment(sketch, "E387", {"start": v(2.3, -6.44) * mm, "end": v(2.33, -6.3) * mm});
            skLineSegment(sketch, "E388", {"start": v(2.33, -6.3) * mm, "end": v(2.34, -6.15) * mm});
            skLineSegment(sketch, "E389", {"start": v(2.34, -6.15) * mm, "end": v(2.34, -6.01) * mm});
            skLineSegment(sketch, "E390", {"start": v(2.34, -6.01) * mm, "end": v(2.34, -5.87) * mm});
            skLineSegment(sketch, "E391", {"start": v(2.34, -5.87) * mm, "end": v(2.33, -5.74) * mm});
            skLineSegment(sketch, "E392", {"start": v(2.33, -5.74) * mm, "end": v(2.32, -5.67) * mm});
            skLineSegment(sketch, "E393", {"start": v(2.32, -5.67) * mm, "end": v(2.3, -5.6) * mm});
            skLineSegment(sketch, "E394", {"start": v(2.3, -5.6) * mm, "end": v(2.29, -5.54) * mm});
            skLineSegment(sketch, "E395", {"start": v(2.29, -5.54) * mm, "end": v(2.27, -5.48) * mm});
            skLineSegment(sketch, "E396", {"start": v(2.27, -5.48) * mm, "end": v(2.27, -5.44) * mm});
            skLineSegment(sketch, "E397", {"start": v(2.27, -5.44) * mm, "end": v(2.26, -5.41) * mm});
            skLineSegment(sketch, "E398", {"start": v(2.26, -5.41) * mm, "end": v(2.26, -5.37) * mm});
            skLineSegment(sketch, "E399", {"start": v(2.26, -5.37) * mm, "end": v(2.27, -5.34) * mm});
            skLineSegment(sketch, "E400", {"start": v(2.27, -5.34) * mm, "end": v(2.94, -4.96) * mm});
            skLineSegment(sketch, "E401", {"start": v(2.94, -4.96) * mm, "end": v(3.58, -4.56) * mm});
            skLineSegment(sketch, "E402", {"start": v(3.58, -4.56) * mm, "end": v(3.62, -4.57) * mm});
            skLineSegment(sketch, "E403", {"start": v(3.62, -4.57) * mm, "end": v(3.65, -4.59) * mm});
            skLineSegment(sketch, "E404", {"start": v(3.65, -4.59) * mm, "end": v(3.68, -4.6) * mm});
            skLineSegment(sketch, "E405", {"start": v(3.68, -4.6) * mm, "end": v(3.7, -4.63) * mm});
            skLineSegment(sketch, "E406", {"start": v(3.7, -4.63) * mm, "end": v(3.75, -4.68) * mm});
            skLineSegment(sketch, "E407", {"start": v(3.75, -4.68) * mm, "end": v(3.8, -4.72) * mm});
            skLineSegment(sketch, "E408", {"start": v(3.8, -4.72) * mm, "end": v(3.85, -4.76) * mm});
            skLineSegment(sketch, "E409", {"start": v(3.85, -4.76) * mm, "end": v(3.9, -4.8) * mm});
            skLineSegment(sketch, "E410", {"start": v(3.9, -4.8) * mm, "end": v(4.02, -4.88) * mm});
            skLineSegment(sketch, "E411", {"start": v(4.02, -4.88) * mm, "end": v(4.14, -4.95) * mm});
            skLineSegment(sketch, "E412", {"start": v(4.14, -4.95) * mm, "end": v(4.27, -5.01) * mm});
            skLineSegment(sketch, "E413", {"start": v(4.27, -5.01) * mm, "end": v(4.4, -5.07) * mm});
            skLineSegment(sketch, "E414", {"start": v(4.4, -5.07) * mm, "end": v(4.54, -5.12) * mm});
            skLineSegment(sketch, "E415", {"start": v(4.54, -5.12) * mm, "end": v(4.68, -5.17) * mm});
            skLineSegment(sketch, "E416", {"start": v(4.68, -5.17) * mm, "end": v(4.83, -5.21) * mm});
            skLineSegment(sketch, "E417", {"start": v(4.83, -5.21) * mm, "end": v(4.98, -5.25) * mm});
            skLineSegment(sketch, "E418", {"start": v(4.98, -5.25) * mm, "end": v(5.14, -5.28) * mm});
            skLineSegment(sketch, "E419", {"start": v(5.14, -5.28) * mm, "end": v(5.3, -5.3) * mm});
            skLineSegment(sketch, "E420", {"start": v(5.3, -5.3) * mm, "end": v(5.46, -5.32) * mm});
            skLineSegment(sketch, "E421", {"start": v(5.46, -5.32) * mm, "end": v(5.59, -5.34) * mm});
            skLineSegment(sketch, "E422", {"start": v(5.59, -5.34) * mm, "end": v(6, -4.87) * mm});
            skLineSegment(sketch, "E423", {"start": v(6, -4.87) * mm, "end": v(5.97, -4.75) * mm});
            skLineSegment(sketch, "E424", {"start": v(5.97, -4.75) * mm, "end": v(5.93, -4.6) * mm});
            skLineSegment(sketch, "E425", {"start": v(5.93, -4.6) * mm, "end": v(5.88, -4.44) * mm});
            skLineSegment(sketch, "E426", {"start": v(5.88, -4.44) * mm, "end": v(5.83, -4.28) * mm});
            skLineSegment(sketch, "E427", {"start": v(5.83, -4.28) * mm, "end": v(5.78, -4.14) * mm});
            skLineSegment(sketch, "E428", {"start": v(5.78, -4.14) * mm, "end": v(5.72, -4) * mm});
            skLineSegment(sketch, "E429", {"start": v(5.72, -4) * mm, "end": v(5.65, -3.86) * mm});
            skSolve(sketch);
        }
        {
            var Q0;
            Q0 = qSketchRegion(id + "F0", true);
            extrude(context, id + "F1", {"entities" : qUnion([Q0]), "depth" : 21 * mm});
        }
        {
            var Q0;
            Q0=qCreatedBy(makeId("Top.planeOp"),FACE);
            var sketch = newSketch(context, id + "F2", { "sketchPlane" : qUnion([Q0])});
            skCircle(sketch, "E430", {"center": v(0, 0) * mm, "radius": 2.6 * mm});
            skSolve(sketch);
        }
        {
            var Q0;
            Q0=qCreatedBy(makeId("Top.planeOp"),FACE);
            var sketch = newSketch(context, id + "F3", { "sketchPlane" : qUnion([Q0])});
            skCircle(sketch, "E431", {"center": v(0, 0) * mm, "radius": 10 * mm});
            skSolve(sketch);
        }
        {
            var Q0;
            Q0 = qSketchRegion(id + "F3", true);
            extrude(context, id + "F4", {"entities" : qUnion([Q0]), "operationType" : NewBodyOperationType.ADD, "oppositeDirection" : true, "depth" : 10 * mm});
        }
        {
            var Q0;
            Q0 = qSketchRegion(id + "F2", true);
            var Q1;
            Q1=sQuery(id+"F2.wireOp",EDGE,"E430");
            extrude(context, id + "F5", {"entities" : qUnion([Q0]), "operationType" : NewBodyOperationType.REMOVE, "surfaceEntities" : qUnion([Q1]), "endBound" : BoundingType.THROUGH_ALL, "depth" : 25 * mm, "hasSecondDirection" : true, "secondDirectionBound" : SecondDirectionBoundingType.THROUGH_ALL, "secondDirectionOppositeDirection" : true, "secondDirectionDepth" : 25 * mm});
        }
        {
            var Q0;
            Q0=makeQuery(id+"F4.opExtrude","CAP_FACE",FACE,{"disambiguationData":[OSD([sQuery(id+"F3.wireOp",EDGE,"E431")])],"isStart":false});
            var sketch = newSketch(context, id + "F6", { "sketchPlane" : qUnion([Q0])});
            skLineSegment(sketch, "E432", {"start": v(0, 0) * mm, "end": v(0, -5.64) * mm, "construction": true});
            skLineSegment(sketch, "E433.bottom", {"start": v(3.25, -3.9) * mm, "end": v(-3.25, -3.9) * mm});
            skLineSegment(sketch, "E433.top", {"start": v(3.25, -7.4) * mm, "end": v(-3.25, -7.4) * mm});
            skLineSegment(sketch, "E433.left", {"start": v(3.25, -3.9) * mm, "end": v(3.25, -7.4) * mm});
            skLineSegment(sketch, "E433.right", {"start": v(-3.25, -3.9) * mm, "end": v(-3.25, -7.4) * mm});
            skPoint(sketch, "E433.middle", {"position": v(0, -5.64) * mm});
            skSolve(sketch);
        }
        {
            var Q0;
            Q0 = qSketchRegion(id + "F6", true);
            extrude(context, id + "F7", {"entities" : qUnion([Q0]), "operationType" : NewBodyOperationType.REMOVE, "oppositeDirection" : true, "depth" : 5 * mm});
        }
        {
            var Q0;
            Q0=qCreatedBy(makeId("Front.planeOp"),FACE);
            var sketch = newSketch(context, id + "F8", { "sketchPlane" : qUnion([Q0])});
            skLineSegment(sketch, "E434", {"start": v(0, 0) * mm, "end": v(0, -10) * mm, "construction": true});
            skCircle(sketch, "E435", {"center": v(0, -5) * mm, "radius": 1.6 * mm});
            skSolve(sketch);
        }
        {
            var Q0;
            Q0 = qSketchRegion(id + "F8", true);
            extrude(context, id + "F9", {"entities" : qUnion([Q0]), "operationType" : NewBodyOperationType.REMOVE, "oppositeDirection" : true, "depth" : 25 * mm});
        }
        {
            var Q0;
            Q0=makeQuery(id+"F7.boolean.opBoolean","COPY",FACE,{"derivedFrom":makeQuery(id+"F7.opExtrude","SWEPT_FACE",FACE,{"disambiguationData":[OSD([sQuery(id+"F6.wireOp",EDGE,"E433.bottom")])]})});
            var sketch = newSketch(context, id + "F10", { "sketchPlane" : qUnion([Q0])});
            skCircle(sketch, "E436.cCircle", {"center": v(0, -5) * mm, "radius": 3.25 * mm, "construction": true});
            skLineSegment(sketch, "E436.0", {"start": v(3.25, -3.12) * mm, "end": v(3.25, -6.88) * mm});
            skLineSegment(sketch, "E436.1", {"start": v(3.25, -6.88) * mm, "end": v(0, -8.75) * mm});
            skLineSegment(sketch, "E436.2", {"start": v(0, -8.75) * mm, "end": v(-3.25, -6.88) * mm});
            skLineSegment(sketch, "E436.3", {"start": v(-3.25, -6.88) * mm, "end": v(-3.25, -3.12) * mm});
            skLineSegment(sketch, "E436.4", {"start": v(-3.25, -3.12) * mm, "end": v(0, -1.25) * mm});
            skLineSegment(sketch, "E436.5", {"start": v(0, -1.25) * mm, "end": v(3.25, -3.12) * mm});
            skPoint(sketch, "E436.0.midPoint", {"position": v(3.25, -5) * mm});
            skSolve(sketch);
        }
        {
            var Q0;
            Q0 = qSketchRegion(id + "F10", true);
            var Q1;
            Q1=makeQuery(id+"F7.boolean.opBoolean","COPY",VERTEX,{"derivedFrom":makeQuery(id+"F7.opExtrude","CAP_VERTEX",VERTEX,{"disambiguationData":[OSD([sQuery(id+"F6.wireOp",EDGE,"E433.top"),sQuery(id+"F6.wireOp",EDGE,"E433.right")])],"isStart":false})});
            extrude(context, id + "F11", {"entities" : qUnion([Q0]), "operationType" : NewBodyOperationType.REMOVE, "endBound" : BoundingType.UP_TO_VERTEX, "endBoundEntityVertex" : qUnion([Q1]), "depth" : 25 * mm});
        }
        {
            var Q0;
            Q0=makeQuery(id+"F4.opExtrude","CAP_EDGE",EDGE,{"disambiguationData":[OSD([sQuery(id+"F3.wireOp",EDGE,"E431")])],"isStart":true});
            chamfer(context, id + "F12", {"entities" : qUnion([Q0]), "width" : 1 * mm, "tangentPropagation" : true});
        }
    });
